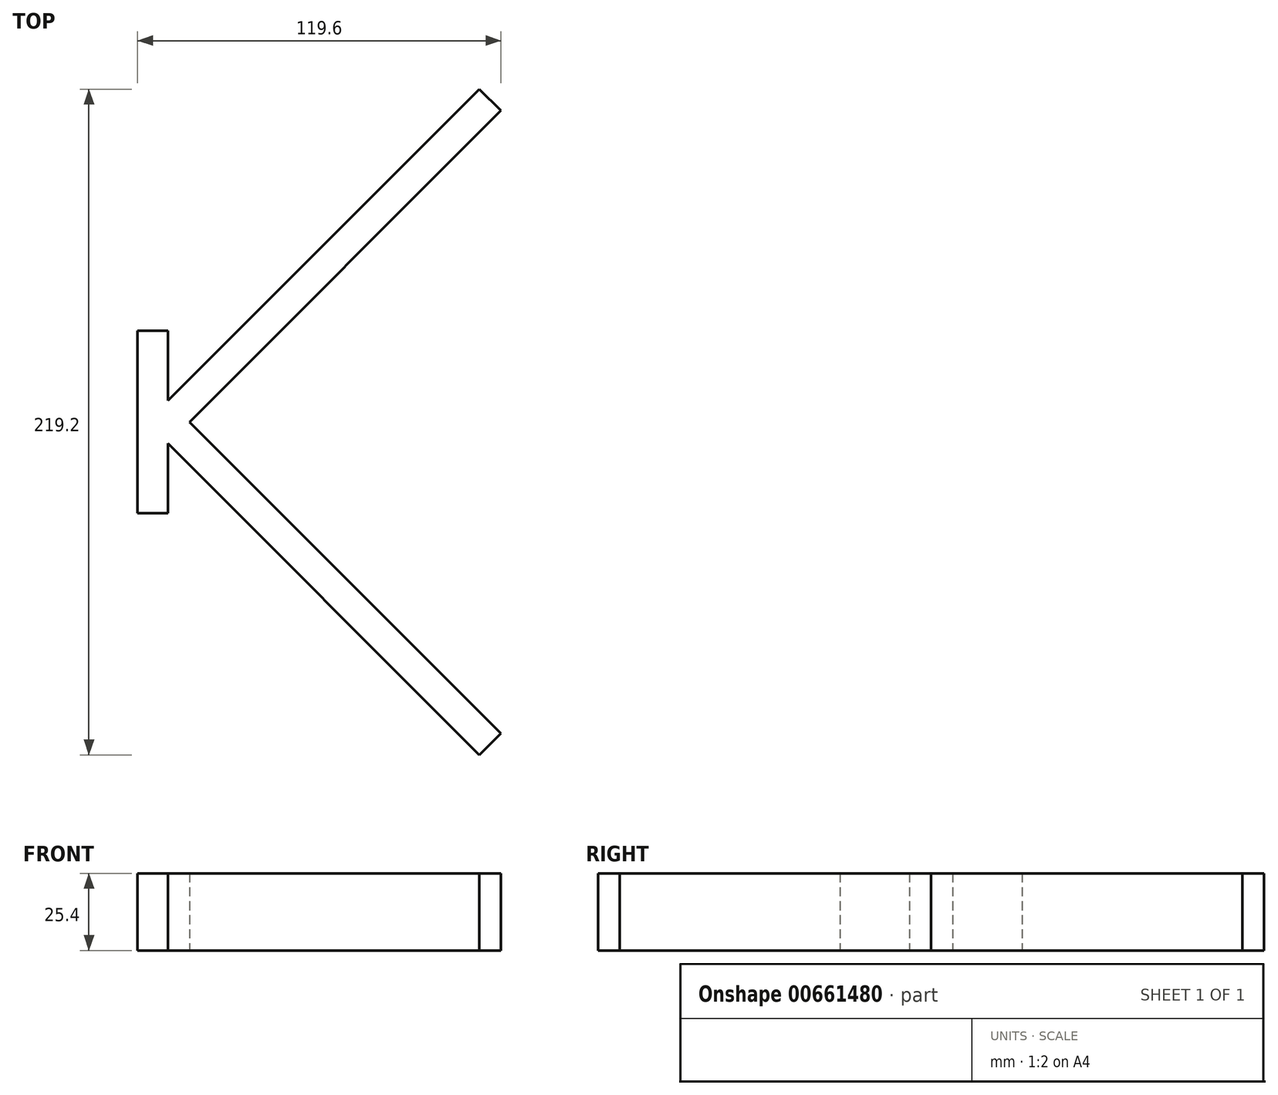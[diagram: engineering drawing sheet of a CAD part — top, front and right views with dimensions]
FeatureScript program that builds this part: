
annotation { "Feature Type Name" : "Feature", "Feature Type Description" : "" }
export const myFeature = defineFeature(function(context is Context, id is Id, definition is map)
    precondition{}
    {
        {
            var Q0;
            Q0=qCreatedBy(makeId("Top.planeOp"),FACE);
            var sketch = newSketch(context, id + "F0", { "sketchPlane" : qUnion([Q0])});
            skLineSegment(sketch, "E0", {"start": v(0, 0) * mm, "end": v(0, 60) * mm});
            skLineSegment(sketch, "E1", {"start": v(0, 30) * mm, "end": v(106.07, 136.07) * mm});
            skLineSegment(sketch, "E2", {"start": v(0, 30) * mm, "end": v(106.07, -76.07) * mm});
            skLineSegment(sketch, "E3", {"start": v(106.07, 136.07) * mm, "end": v(102.53, 139.6) * mm});
            skLineSegment(sketch, "E4", {"start": v(102.53, 139.6) * mm, "end": v(0, 37.07) * mm});
            skLineSegment(sketch, "E5", {"start": v(106.07, -76.07) * mm, "end": v(102.53, -79.6) * mm});
            skLineSegment(sketch, "E6", {"start": v(102.53, -79.6) * mm, "end": v(0, 22.93) * mm});
            skLineSegment(sketch, "E7", {"start": v(106.07, 136.07) * mm, "end": v(109.6, 132.53) * mm});
            skLineSegment(sketch, "E8", {"start": v(109.6, 132.53) * mm, "end": v(7.07, 30) * mm});
            skLineSegment(sketch, "E9", {"start": v(7.07, 30) * mm, "end": v(109.6, -72.53) * mm});
            skLineSegment(sketch, "E10", {"start": v(109.6, -72.53) * mm, "end": v(106.07, -76.07) * mm});
            skLineSegment(sketch, "E11", {"start": v(0, 0) * mm, "end": v(-10, 0) * mm});
            skLineSegment(sketch, "E12", {"start": v(-10, 0) * mm, "end": v(-10, 60) * mm});
            skLineSegment(sketch, "E13", {"start": v(-10, 60) * mm, "end": v(0, 60) * mm});
            skSolve(sketch);
        }
        {
            var Q0;
            Q0=makeQuery(id+"F0.imprint","IMPRINT",FACE,{"disambiguationData":[TD([[makeQuery(id+"F0.imprint","IMPRINT",EDGE,{"derivedFrom":sQuery(id+"F0.wireOp",EDGE,"E1")}),-1.0]])]});
            extrude(context, id + "F1", {"entities" : qUnion([Q0]), "depth" : 12.7 * mm, "offsetDistance" : 25.4 * mm});
        }
        {
            var Q0;
            Q0 = qSketchRegion(id + "F0", true);
            extrude(context, id + "F2", {"entities" : qUnion([Q0]), "operationType" : NewBodyOperationType.ADD, "depth" : 25.4 * mm, "offsetDistance" : 25.4 * mm});
        }
    });
